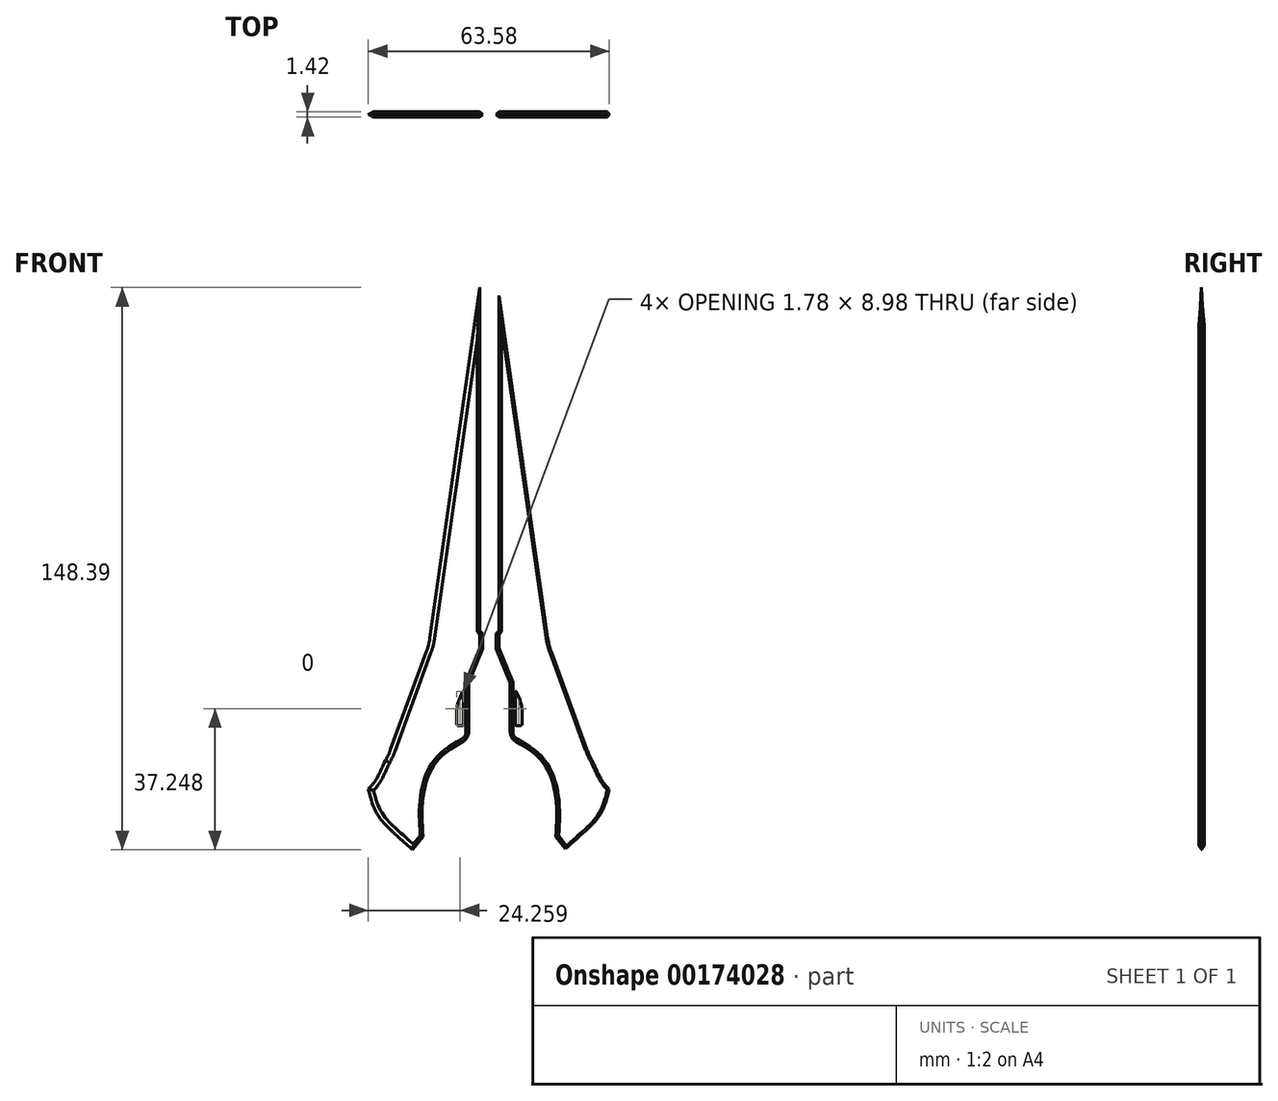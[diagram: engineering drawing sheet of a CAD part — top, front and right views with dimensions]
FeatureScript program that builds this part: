
annotation { "Feature Type Name" : "Feature", "Feature Type Description" : "" }
export const myFeature = defineFeature(function(context is Context, id is Id, definition is map)
    precondition{}
    {
        {
            var Q0;
            Q0=qCreatedBy(makeId("Front.planeOp"),FACE);
            var sketch = newSketch(context, id + "F0", { "sketchPlane" : qUnion([Q0])});
            skLineSegment(sketch, "E0", {"start": v(-25.5, 85.22) * mm, "end": v(-25.5, 20.45) * mm});
            skLineSegment(sketch, "E1", {"start": v(-25.5, 20.45) * mm, "end": v(-24.98, 19.9) * mm});
            skLineSegment(sketch, "E2", {"start": v(-24.98, 19.9) * mm, "end": v(-24.98, 17.1) * mm});
            skLineSegment(sketch, "E3", {"start": v(-24.98, 17.1) * mm, "end": v(-27.64, 10.64) * mm});
            skLineSegment(sketch, "E4", {"start": v(-27.64, 10.64) * mm, "end": v(-27.64, 1.36) * mm});
            skLineSegment(sketch, "E5", {"start": v(-25.5, 85.22) * mm, "end": v(-34.93, 19.12) * mm});
            skLineSegment(sketch, "E6", {"start": v(-35.58, 16.54) * mm, "end": v(-42.37, -1.97) * mm});
            skLineSegment(sketch, "E7", {"start": v(-38.2, -20.82) * mm, "end": v(-36.23, -18.34) * mm});
            skPoint(sketch, "E8.visualSharp", {"position": v(-35.12, 17.8) * mm});
            skArc(sketch, "E8.filletArc", {"start": v(-35.58, 16.54) * mm, "mid": v(-35.19, 17.82) * mm, "end": v(-34.93, 19.12) * mm});
            skPoint(sketch, "E9.visualSharp", {"position": v(-42.76, -3.04) * mm});
            skArc(sketch, "E9.filletArc", {"start": v(-43.33, -4.01) * mm, "mid": v(-42.8, -3.01) * mm, "end": v(-42.37, -1.97) * mm});
            skFitSpline(sketch, "E10", {"points": [v(-46.54, -9.4) * mm, v(-44.6, -14.54) * mm, v(-38.2, -20.82) * mm], "startDerivative": vector(3.06, -11.58) * mm, "endDerivative": vector(12.95, -11.95) * mm});
            skFitSpline(sketch, "E11", {"points": [v(-43.33, -4.01) * mm, v(-45.27, -7.9) * mm, v(-46.54, -9.4) * mm], "startDerivative": vector(-3.3, -7.32) * mm, "endDerivative": vector(-3.1, -3.4) * mm});
            skFitSpline(sketch, "E12", {"points": [v(-36.23, -18.34) * mm, v(-36.23, -10.9) * mm, v(-33.6, -4.1) * mm, v(-27.64, 0.16) * mm], "startDerivative": vector(-1.67, 22.09) * mm, "endDerivative": vector(19.97, 10.9) * mm});
            skArc(sketch, "E13.filletArc", {"start": v(-28.69, -0.41) * mm, "mid": v(-27.92, 0.33) * mm, "end": v(-27.64, 1.36) * mm});
            skLineSegment(sketch, "E14", {"start": v(-28.58, 9.5) * mm, "end": v(-29.85, 6.42) * mm});
            skLineSegment(sketch, "E15", {"start": v(-29.85, 6.42) * mm, "end": v(-29.85, 2.58) * mm});
            skLineSegment(sketch, "E16", {"start": v(-29.85, 2.58) * mm, "end": v(-28.58, 2.58) * mm});
            skLineSegment(sketch, "E17", {"start": v(-28.58, 2.58) * mm, "end": v(-28.58, 9.5) * mm});
            skLineSegment(sketch, "E18", {"start": v(-23.71, 22.02) * mm, "end": v(-23.71, 15.34) * mm, "construction": true});
            skLineSegment(sketch, "E19.MirrorCS", {"start": v(-21.92, 85.22) * mm, "end": v(-21.92, 20.45) * mm});
            skLineSegment(sketch, "E20.MirrorCS", {"start": v(-21.92, 20.45) * mm, "end": v(-22.44, 19.9) * mm});
            skLineSegment(sketch, "E21.MirrorCS", {"start": v(-22.44, 19.9) * mm, "end": v(-22.44, 17.1) * mm});
            skLineSegment(sketch, "E22.MirrorCS", {"start": v(-22.44, 17.1) * mm, "end": v(-19.79, 10.64) * mm});
            skLineSegment(sketch, "E23.MirrorCS", {"start": v(-19.79, 10.64) * mm, "end": v(-19.79, 1.36) * mm});
            skLineSegment(sketch, "E24.MirrorCS", {"start": v(-18.85, 2.58) * mm, "end": v(-18.85, 9.5) * mm});
            skLineSegment(sketch, "E25.MirrorCS", {"start": v(-18.85, 9.5) * mm, "end": v(-17.58, 6.42) * mm});
            skLineSegment(sketch, "E26.MirrorCS", {"start": v(-17.58, 6.42) * mm, "end": v(-17.58, 2.58) * mm});
            skLineSegment(sketch, "E27.MirrorCS", {"start": v(-17.58, 2.58) * mm, "end": v(-18.85, 2.58) * mm});
            skArc(sketch, "E28.MirrorCS", {"start": v(-18.74, -0.41) * mm, "mid": v(-19.5, 0.33) * mm, "end": v(-19.79, 1.36) * mm});
            skFitSpline(sketch, "E29.MirrorCS", {"points": [v(-11.2, -18.34) * mm, v(-11.2, -10.9) * mm, v(-13.83, -4.1) * mm, v(-19.79, 0.16) * mm], "startDerivative": vector(1.67, 22.09) * mm, "endDerivative": vector(-19.97, 10.9) * mm});
            skLineSegment(sketch, "E30.MirrorCS", {"start": v(-9.22, -20.82) * mm, "end": v(-11.2, -18.34) * mm});
            skFitSpline(sketch, "E31.MirrorCS", {"points": [v(-0.89, -9.4) * mm, v(-2.84, -14.54) * mm, v(-9.22, -20.82) * mm], "startDerivative": vector(-3.06, -11.58) * mm, "endDerivative": vector(-12.95, -11.95) * mm});
            skFitSpline(sketch, "E32.MirrorCS", {"points": [v(-4.1, -4.01) * mm, v(-2.16, -7.9) * mm, v(-0.89, -9.4) * mm], "startDerivative": vector(3.3, -7.32) * mm, "endDerivative": vector(3.1, -3.4) * mm});
            skArc(sketch, "E33.MirrorCS", {"start": v(-4.1, -4.01) * mm, "mid": v(-4.62, -3.01) * mm, "end": v(-5.06, -1.97) * mm});
            skLineSegment(sketch, "E34.MirrorCS", {"start": v(-11.85, 16.54) * mm, "end": v(-5.06, -1.97) * mm});
            skArc(sketch, "E35.MirrorCS", {"start": v(-11.85, 16.54) * mm, "mid": v(-12.24, 17.82) * mm, "end": v(-12.5, 19.12) * mm});
            skLineSegment(sketch, "E36.MirrorCS", {"start": v(-21.92, 85.22) * mm, "end": v(-12.5, 19.12) * mm});
            skSolve(sketch);
        }
        {
            var Q0;
            Q0 = qSketchRegion(id + "F0", true);
            extrude(context, id + "F1", {"entities" : qUnion([Q0]), "depth" : 0.5 * mm});
        }
        {
            var Q0;
            Q0=makeQuery(id+"F1.opExtrude","SWEPT_EDGE",EDGE,{"disambiguationData":[OSD([sQuery(id+"F0.wireOp",EDGE,"E14"),sQuery(id+"F0.wireOp",EDGE,"E15")])]});
            fillet(context, id + "F2", {"entities" : qUnion([Q0]), "radius" : 5.08 * mm, "tangentPropagation" : true, "allowEdgeOverflow" : false});
        }
        {
            var Q0;
            Q0=makeQuery(id+"F1.opExtrude","SWEPT_EDGE",EDGE,{"disambiguationData":[OSD([sQuery(id+"F0.wireOp",EDGE,"E15"),sQuery(id+"F0.wireOp",EDGE,"E16")])]});
            var Q1;
            Q1=makeQuery(id+"F1.opExtrude","SWEPT_EDGE",EDGE,{"disambiguationData":[OSD([sQuery(id+"F0.wireOp",EDGE,"E16"),sQuery(id+"F0.wireOp",EDGE,"E17")])]});
            fillet(context, id + "F3", {"entities" : qUnion([Q0, Q1]), "radius" : 0.25 * mm, "tangentPropagation" : true, "allowEdgeOverflow" : false});
        }
        {
            var Q0;
            Q0=makeQuery(id+"F1.opExtrude","SWEPT_EDGE",EDGE,{"disambiguationData":[OSD([sQuery(id+"F0.wireOp",EDGE,"E14"),sQuery(id+"F0.wireOp",EDGE,"E17")])]});
            var Q1;
            Q1=makeQuery(id+"F1.opExtrude","SWEPT_EDGE",EDGE,{"disambiguationData":[OSD([sQuery(id+"F0.wireOp",EDGE,"E24.MirrorCS"),sQuery(id+"F0.wireOp",EDGE,"E25.MirrorCS")])]});
            fillet(context, id + "F4", {"entities" : qUnion([Q0, Q1]), "radius" : 0.13 * mm, "tangentPropagation" : true, "allowEdgeOverflow" : false});
        }
        {
            var Q0;
            Q0=makeQuery(id+"F1.opExtrude","CAP_EDGE",EDGE,{"disambiguationData":[OSD([sQuery(id+"F0.wireOp",EDGE,"E0")])],"isStart":false});
            var Q1;
            Q1=makeQuery(id+"F1.opExtrude","CAP_EDGE",EDGE,{"disambiguationData":[OSD([sQuery(id+"F0.wireOp",EDGE,"E1")])],"isStart":false});
            var Q2;
            Q2=makeQuery(id+"F1.opExtrude","CAP_EDGE",EDGE,{"disambiguationData":[OSD([sQuery(id+"F0.wireOp",EDGE,"E2")])],"isStart":false});
            var Q3;
            Q3=makeQuery(id+"F1.opExtrude","CAP_EDGE",EDGE,{"disambiguationData":[OSD([sQuery(id+"F0.wireOp",EDGE,"E3")])],"isStart":false});
            var Q4;
            Q4=makeQuery(id+"F1.opExtrude","CAP_EDGE",EDGE,{"disambiguationData":[OSD([sQuery(id+"F0.wireOp",EDGE,"E4")])],"isStart":false});
            var Q5;
            Q5=makeQuery(id+"F1.opExtrude","CAP_EDGE",EDGE,{"disambiguationData":[OSD([sQuery(id+"F0.wireOp",EDGE,"E13.filletArc")])],"isStart":false});
            var Q6;
            Q6=makeQuery(id+"F1.opExtrude","CAP_EDGE",EDGE,{"disambiguationData":[OSD([sQuery(id+"F0.wireOp",EDGE,"E12")])],"isStart":false});
            var Q7;
            Q7=makeQuery(id+"F1.opExtrude","CAP_EDGE",EDGE,{"disambiguationData":[OSD([sQuery(id+"F0.wireOp",EDGE,"E7")])],"isStart":false});
            var Q8;
            Q8=makeQuery(id+"F1.opExtrude","CAP_EDGE",EDGE,{"disambiguationData":[OSD([sQuery(id+"F0.wireOp",EDGE,"E19.MirrorCS")])],"isStart":false});
            var Q9;
            Q9=makeQuery(id+"F1.opExtrude","CAP_EDGE",EDGE,{"disambiguationData":[OSD([sQuery(id+"F0.wireOp",EDGE,"E21.MirrorCS")])],"isStart":false});
            var Q10;
            Q10=makeQuery(id+"F1.opExtrude","CAP_EDGE",EDGE,{"disambiguationData":[OSD([sQuery(id+"F0.wireOp",EDGE,"E20.MirrorCS")])],"isStart":false});
            var Q11;
            Q11=makeQuery(id+"F1.opExtrude","CAP_EDGE",EDGE,{"disambiguationData":[OSD([sQuery(id+"F0.wireOp",EDGE,"E22.MirrorCS")])],"isStart":false});
            var Q12;
            Q12=makeQuery(id+"F1.opExtrude","CAP_EDGE",EDGE,{"disambiguationData":[OSD([sQuery(id+"F0.wireOp",EDGE,"E23.MirrorCS")])],"isStart":false});
            var Q13;
            Q13=makeQuery(id+"F1.opExtrude","CAP_EDGE",EDGE,{"disambiguationData":[OSD([sQuery(id+"F0.wireOp",EDGE,"E28.MirrorCS")])],"isStart":false});
            var Q14;
            Q14=makeQuery(id+"F1.opExtrude","CAP_EDGE",EDGE,{"disambiguationData":[OSD([sQuery(id+"F0.wireOp",EDGE,"E29.MirrorCS")])],"isStart":false});
            var Q15;
            Q15=makeQuery(id+"F1.opExtrude","CAP_EDGE",EDGE,{"disambiguationData":[OSD([sQuery(id+"F0.wireOp",EDGE,"E30.MirrorCS")])],"isStart":false});
            chamfer(context, id + "F5", {"entities" : qUnion([Q0, Q1, Q2, Q3, Q4, Q5, Q6, Q7, Q8, Q9, Q10, Q11, Q12, Q13, Q14, Q15]), "width" : 0.5 * mm, "tangentPropagation" : true});
        }
        {
            var Q0;
            Q0=makeQuery(id+"F1.opExtrude","CAP_EDGE",EDGE,{"disambiguationData":[OSD([sQuery(id+"F0.wireOp",EDGE,"E10")])],"isStart":false});
            var Q1;
            Q1=makeQuery(id+"F1.opExtrude","CAP_EDGE",EDGE,{"disambiguationData":[OSD([sQuery(id+"F0.wireOp",EDGE,"E11")])],"isStart":false});
            var Q2;
            Q2=makeQuery(id+"F1.opExtrude","CAP_EDGE",EDGE,{"disambiguationData":[OSD([sQuery(id+"F0.wireOp",EDGE,"E5")])],"isStart":false});
            var Q3;
            Q3=makeQuery(id+"F1.opExtrude","CAP_EDGE",EDGE,{"disambiguationData":[OSD([sQuery(id+"F0.wireOp",EDGE,"E35.MirrorCS")])],"isStart":false});
            var Q4;
            Q4=makeQuery(id+"F1.opExtrude","CAP_EDGE",EDGE,{"disambiguationData":[OSD([sQuery(id+"F0.wireOp",EDGE,"E32.MirrorCS")])],"isStart":false});
            var Q5;
            Q5=makeQuery(id+"F1.opExtrude","CAP_EDGE",EDGE,{"disambiguationData":[OSD([sQuery(id+"F0.wireOp",EDGE,"E31.MirrorCS")])],"isStart":false});
            chamfer(context, id + "F6", {"entities" : qUnion([Q0, Q1, Q2, Q3, Q4, Q5]), "chamferType" : ChamferType.OFFSET_ANGLE, "width" : 0.89 * mm, "oppositeDirection" : false, "angle" : 30 * degree, "tangentPropagation" : true});
        }
        {
            var Q0;
            Q0=makeQuery(id+"F1.opExtrude","SWEPT_BODY",BODY,{"disambiguationData":[OSD([sQuery(id+"F0.wireOp",EDGE,"E0"),sQuery(id+"F0.wireOp",EDGE,"E1"),sQuery(id+"F0.wireOp",EDGE,"E2"),sQuery(id+"F0.wireOp",EDGE,"E3"),sQuery(id+"F0.wireOp",EDGE,"E4"),sQuery(id+"F0.wireOp",EDGE,"E5"),sQuery(id+"F0.wireOp",EDGE,"E6"),sQuery(id+"F0.wireOp",EDGE,"E7"),sQuery(id+"F0.wireOp",EDGE,"E8.filletArc"),sQuery(id+"F0.wireOp",EDGE,"E9.filletArc"),sQuery(id+"F0.wireOp",EDGE,"E10"),sQuery(id+"F0.wireOp",EDGE,"E11"),sQuery(id+"F0.wireOp",EDGE,"E12"),sQuery(id+"F0.wireOp",EDGE,"E13.filletArc"),sQuery(id+"F0.wireOp",EDGE,"E14"),sQuery(id+"F0.wireOp",EDGE,"E15"),sQuery(id+"F0.wireOp",EDGE,"E16"),sQuery(id+"F0.wireOp",EDGE,"E17")])]});
            var Q1;
            Q1=makeQuery(id+"F1.opExtrude","CAP_FACE",FACE,{"disambiguationData":[OSD([sQuery(id+"F0.wireOp",EDGE,"E0"),sQuery(id+"F0.wireOp",EDGE,"E1"),sQuery(id+"F0.wireOp",EDGE,"E2"),sQuery(id+"F0.wireOp",EDGE,"E3"),sQuery(id+"F0.wireOp",EDGE,"E4"),sQuery(id+"F0.wireOp",EDGE,"E5"),sQuery(id+"F0.wireOp",EDGE,"E6"),sQuery(id+"F0.wireOp",EDGE,"E7"),sQuery(id+"F0.wireOp",EDGE,"E8.filletArc"),sQuery(id+"F0.wireOp",EDGE,"E9.filletArc"),sQuery(id+"F0.wireOp",EDGE,"E10"),sQuery(id+"F0.wireOp",EDGE,"E11"),sQuery(id+"F0.wireOp",EDGE,"E12"),sQuery(id+"F0.wireOp",EDGE,"E13.filletArc"),sQuery(id+"F0.wireOp",EDGE,"E14"),sQuery(id+"F0.wireOp",EDGE,"E15"),sQuery(id+"F0.wireOp",EDGE,"E16"),sQuery(id+"F0.wireOp",EDGE,"E17")])],"isStart":true});
            mirror(context, id + "F7", {"entities" : qUnion([Q0]), "mirrorPlane" : qUnion([Q1])});
        }
        {
            var Q0;
            Q0=makeQuery(id+"F1.opExtrude","SWEPT_BODY",BODY,{"disambiguationData":[OSD([sQuery(id+"F0.wireOp",EDGE,"E19.MirrorCS"),sQuery(id+"F0.wireOp",EDGE,"E20.MirrorCS"),sQuery(id+"F0.wireOp",EDGE,"E21.MirrorCS"),sQuery(id+"F0.wireOp",EDGE,"E22.MirrorCS"),sQuery(id+"F0.wireOp",EDGE,"E24.MirrorCS"),sQuery(id+"F0.wireOp",EDGE,"E25.MirrorCS"),sQuery(id+"F0.wireOp",EDGE,"E26.MirrorCS"),sQuery(id+"F0.wireOp",EDGE,"E27.MirrorCS"),sQuery(id+"F0.wireOp",EDGE,"E23.MirrorCS"),sQuery(id+"F0.wireOp",EDGE,"E28.MirrorCS"),sQuery(id+"F0.wireOp",EDGE,"E29.MirrorCS"),sQuery(id+"F0.wireOp",EDGE,"E30.MirrorCS"),sQuery(id+"F0.wireOp",EDGE,"E31.MirrorCS"),sQuery(id+"F0.wireOp",EDGE,"E32.MirrorCS"),sQuery(id+"F0.wireOp",EDGE,"E33.MirrorCS"),sQuery(id+"F0.wireOp",EDGE,"E34.MirrorCS"),sQuery(id+"F0.wireOp",EDGE,"E35.MirrorCS"),sQuery(id+"F0.wireOp",EDGE,"E36.MirrorCS")])]});
            var Q1;
            Q1=makeQuery(id+"F1.opExtrude","CAP_FACE",FACE,{"disambiguationData":[OSD([sQuery(id+"F0.wireOp",EDGE,"E19.MirrorCS"),sQuery(id+"F0.wireOp",EDGE,"E20.MirrorCS"),sQuery(id+"F0.wireOp",EDGE,"E21.MirrorCS"),sQuery(id+"F0.wireOp",EDGE,"E22.MirrorCS"),sQuery(id+"F0.wireOp",EDGE,"E24.MirrorCS"),sQuery(id+"F0.wireOp",EDGE,"E25.MirrorCS"),sQuery(id+"F0.wireOp",EDGE,"E26.MirrorCS"),sQuery(id+"F0.wireOp",EDGE,"E27.MirrorCS"),sQuery(id+"F0.wireOp",EDGE,"E23.MirrorCS"),sQuery(id+"F0.wireOp",EDGE,"E28.MirrorCS"),sQuery(id+"F0.wireOp",EDGE,"E29.MirrorCS"),sQuery(id+"F0.wireOp",EDGE,"E30.MirrorCS"),sQuery(id+"F0.wireOp",EDGE,"E31.MirrorCS"),sQuery(id+"F0.wireOp",EDGE,"E32.MirrorCS"),sQuery(id+"F0.wireOp",EDGE,"E33.MirrorCS"),sQuery(id+"F0.wireOp",EDGE,"E34.MirrorCS"),sQuery(id+"F0.wireOp",EDGE,"E35.MirrorCS"),sQuery(id+"F0.wireOp",EDGE,"E36.MirrorCS")])],"isStart":true});
            mirror(context, id + "F8", {"entities" : qUnion([Q0]), "mirrorPlane" : qUnion([Q1])});
        }
        {
            var Q0;
            {var subQ0=makeQuery(id+"F1.opExtrude","SWEPT_EDGE",EDGE,{"disambiguationData":[OSD([sQuery(id+"F0.wireOp",EDGE,"E25.MirrorCS"),sQuery(id+"F0.wireOp",EDGE,"E26.MirrorCS")])]});Q0=makeQuery(id+"F8.boolean.opBoolean","MERGE",EDGE,{"derivedFrom":[subQ0,makeQuery(id+"F8.opPattern","COPY",EDGE,{"derivedFrom":subQ0,"instanceName":"1"})]});}
            fillet(context, id + "F9", {"entities" : qUnion([Q0]), "radius" : 5.08 * mm, "tangentPropagation" : true, "allowEdgeOverflow" : false});
        }
        {
            var Q0;
            {var subQ0=makeQuery(id+"F1.opExtrude","SWEPT_EDGE",EDGE,{"disambiguationData":[OSD([sQuery(id+"F0.wireOp",EDGE,"E24.MirrorCS"),sQuery(id+"F0.wireOp",EDGE,"E27.MirrorCS")])]});Q0=makeQuery(id+"F8.boolean.opBoolean","MERGE",EDGE,{"derivedFrom":[subQ0,makeQuery(id+"F8.opPattern","COPY",EDGE,{"derivedFrom":subQ0,"instanceName":"1"})]});}
            var Q1;
            {var subQ0=makeQuery(id+"F1.opExtrude","SWEPT_EDGE",EDGE,{"disambiguationData":[OSD([sQuery(id+"F0.wireOp",EDGE,"E26.MirrorCS"),sQuery(id+"F0.wireOp",EDGE,"E27.MirrorCS")])]});Q1=makeQuery(id+"F8.boolean.opBoolean","MERGE",EDGE,{"derivedFrom":[subQ0,makeQuery(id+"F8.opPattern","COPY",EDGE,{"derivedFrom":subQ0,"instanceName":"1"})]});}
            fillet(context, id + "F10", {"entities" : qUnion([Q0, Q1]), "radius" : 0.25 * mm, "tangentPropagation" : true, "allowEdgeOverflow" : false});
        }
        {
            var Q0;
            Q0=makeQuery(id+"F1.opExtrude","SWEPT_BODY",BODY,{"disambiguationData":[OSD([sQuery(id+"F0.wireOp",EDGE,"E0"),sQuery(id+"F0.wireOp",EDGE,"E1"),sQuery(id+"F0.wireOp",EDGE,"E2"),sQuery(id+"F0.wireOp",EDGE,"E3"),sQuery(id+"F0.wireOp",EDGE,"E4"),sQuery(id+"F0.wireOp",EDGE,"E5"),sQuery(id+"F0.wireOp",EDGE,"E6"),sQuery(id+"F0.wireOp",EDGE,"E7"),sQuery(id+"F0.wireOp",EDGE,"E8.filletArc"),sQuery(id+"F0.wireOp",EDGE,"E9.filletArc"),sQuery(id+"F0.wireOp",EDGE,"E10"),sQuery(id+"F0.wireOp",EDGE,"E11"),sQuery(id+"F0.wireOp",EDGE,"E12"),sQuery(id+"F0.wireOp",EDGE,"E13.filletArc"),sQuery(id+"F0.wireOp",EDGE,"E14"),sQuery(id+"F0.wireOp",EDGE,"E15"),sQuery(id+"F0.wireOp",EDGE,"E16"),sQuery(id+"F0.wireOp",EDGE,"E17")])]});
            var Q1;
            Q1=makeQuery(id+"F1.opExtrude","SWEPT_BODY",BODY,{"disambiguationData":[OSD([sQuery(id+"F0.wireOp",EDGE,"E19.MirrorCS"),sQuery(id+"F0.wireOp",EDGE,"E20.MirrorCS"),sQuery(id+"F0.wireOp",EDGE,"E21.MirrorCS"),sQuery(id+"F0.wireOp",EDGE,"E22.MirrorCS"),sQuery(id+"F0.wireOp",EDGE,"E24.MirrorCS"),sQuery(id+"F0.wireOp",EDGE,"E25.MirrorCS"),sQuery(id+"F0.wireOp",EDGE,"E26.MirrorCS"),sQuery(id+"F0.wireOp",EDGE,"E27.MirrorCS"),sQuery(id+"F0.wireOp",EDGE,"E23.MirrorCS"),sQuery(id+"F0.wireOp",EDGE,"E28.MirrorCS"),sQuery(id+"F0.wireOp",EDGE,"E29.MirrorCS"),sQuery(id+"F0.wireOp",EDGE,"E30.MirrorCS"),sQuery(id+"F0.wireOp",EDGE,"E31.MirrorCS"),sQuery(id+"F0.wireOp",EDGE,"E32.MirrorCS"),sQuery(id+"F0.wireOp",EDGE,"E33.MirrorCS"),sQuery(id+"F0.wireOp",EDGE,"E34.MirrorCS"),sQuery(id+"F0.wireOp",EDGE,"E35.MirrorCS"),sQuery(id+"F0.wireOp",EDGE,"E36.MirrorCS")])]});
            var Q2;
            Q2=makeQuery(id+"F7.opPattern","COPY",BODY,{"derivedFrom":makeQuery(id+"F1.opExtrude","SWEPT_BODY",BODY,{"disambiguationData":[OSD([sQuery(id+"F0.wireOp",EDGE,"E0"),sQuery(id+"F0.wireOp",EDGE,"E1"),sQuery(id+"F0.wireOp",EDGE,"E2"),sQuery(id+"F0.wireOp",EDGE,"E3"),sQuery(id+"F0.wireOp",EDGE,"E4"),sQuery(id+"F0.wireOp",EDGE,"E5"),sQuery(id+"F0.wireOp",EDGE,"E6"),sQuery(id+"F0.wireOp",EDGE,"E7"),sQuery(id+"F0.wireOp",EDGE,"E8.filletArc"),sQuery(id+"F0.wireOp",EDGE,"E9.filletArc"),sQuery(id+"F0.wireOp",EDGE,"E10"),sQuery(id+"F0.wireOp",EDGE,"E11"),sQuery(id+"F0.wireOp",EDGE,"E12"),sQuery(id+"F0.wireOp",EDGE,"E13.filletArc"),sQuery(id+"F0.wireOp",EDGE,"E14"),sQuery(id+"F0.wireOp",EDGE,"E15"),sQuery(id+"F0.wireOp",EDGE,"E16"),sQuery(id+"F0.wireOp",EDGE,"E17")])]}),"instanceName":"1"});
            var Q3;
            Q3=makeQuery(id+"F8.opPattern","COPY",BODY,{"derivedFrom":makeQuery(id+"F1.opExtrude","SWEPT_BODY",BODY,{"disambiguationData":[OSD([sQuery(id+"F0.wireOp",EDGE,"E19.MirrorCS"),sQuery(id+"F0.wireOp",EDGE,"E20.MirrorCS"),sQuery(id+"F0.wireOp",EDGE,"E21.MirrorCS"),sQuery(id+"F0.wireOp",EDGE,"E22.MirrorCS"),sQuery(id+"F0.wireOp",EDGE,"E24.MirrorCS"),sQuery(id+"F0.wireOp",EDGE,"E25.MirrorCS"),sQuery(id+"F0.wireOp",EDGE,"E26.MirrorCS"),sQuery(id+"F0.wireOp",EDGE,"E27.MirrorCS"),sQuery(id+"F0.wireOp",EDGE,"E23.MirrorCS"),sQuery(id+"F0.wireOp",EDGE,"E28.MirrorCS"),sQuery(id+"F0.wireOp",EDGE,"E29.MirrorCS"),sQuery(id+"F0.wireOp",EDGE,"E30.MirrorCS"),sQuery(id+"F0.wireOp",EDGE,"E31.MirrorCS"),sQuery(id+"F0.wireOp",EDGE,"E32.MirrorCS"),sQuery(id+"F0.wireOp",EDGE,"E33.MirrorCS"),sQuery(id+"F0.wireOp",EDGE,"E34.MirrorCS"),sQuery(id+"F0.wireOp",EDGE,"E35.MirrorCS"),sQuery(id+"F0.wireOp",EDGE,"E36.MirrorCS")])]}),"instanceName":"1"});
            var Q4;
            Q4=qCreatedBy(makeId("Origin.pointOp"),VERTEX);
            transform(context, id + "F11", {"entities" : qUnion([Q0, Q1, Q2, Q3]), "transformType" : TransformType.SCALE_UNIFORMLY, "scale" : 1.4, "scalePoint" : qUnion([Q4]), "makeCopy" : false});
        }
        {
            var Q0;
            Q0=makeQuery(id+"F1.opExtrude","CAP_FACE",FACE,{"disambiguationData":[OSD([sQuery(id+"F0.wireOp",EDGE,"E0"),sQuery(id+"F0.wireOp",EDGE,"E1"),sQuery(id+"F0.wireOp",EDGE,"E2"),sQuery(id+"F0.wireOp",EDGE,"E3"),sQuery(id+"F0.wireOp",EDGE,"E4"),sQuery(id+"F0.wireOp",EDGE,"E5"),sQuery(id+"F0.wireOp",EDGE,"E6"),sQuery(id+"F0.wireOp",EDGE,"E7"),sQuery(id+"F0.wireOp",EDGE,"E8.filletArc"),sQuery(id+"F0.wireOp",EDGE,"E9.filletArc"),sQuery(id+"F0.wireOp",EDGE,"E10"),sQuery(id+"F0.wireOp",EDGE,"E11"),sQuery(id+"F0.wireOp",EDGE,"E12"),sQuery(id+"F0.wireOp",EDGE,"E13.filletArc"),sQuery(id+"F0.wireOp",EDGE,"E14"),sQuery(id+"F0.wireOp",EDGE,"E15"),sQuery(id+"F0.wireOp",EDGE,"E16"),sQuery(id+"F0.wireOp",EDGE,"E17")])],"isStart":false});
            cPlane(context, id + "F12", {"entities" : qUnion([Q0]), "cplaneType" : CPlaneType.OFFSET, "offset" : 25.4 * mm, "width" : 152.4 * mm, "height" : 152.4 * mm});
        }
    });
